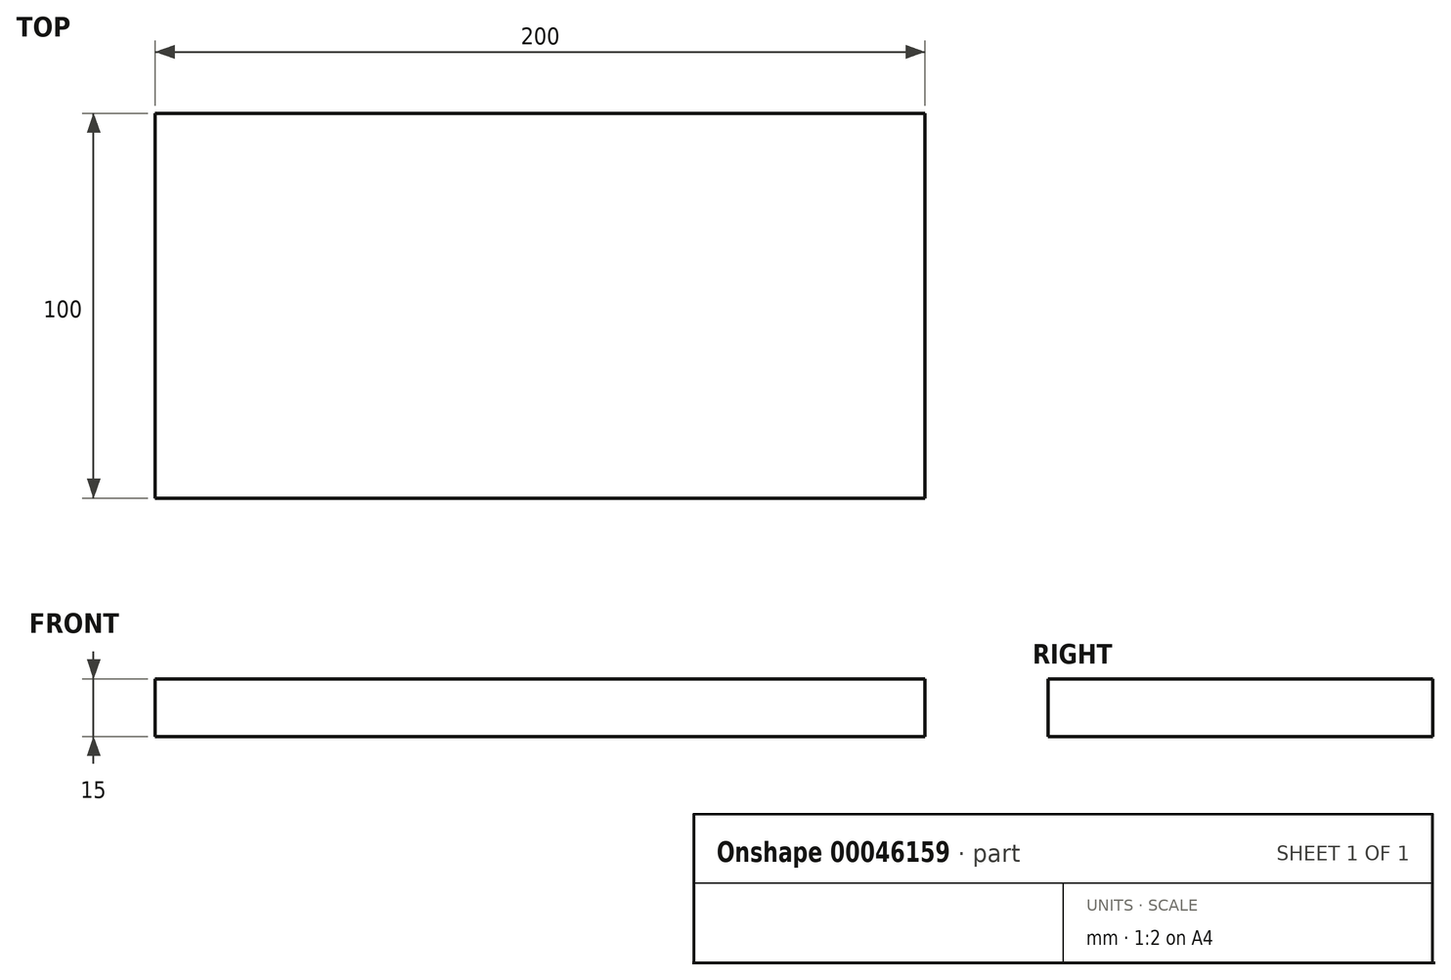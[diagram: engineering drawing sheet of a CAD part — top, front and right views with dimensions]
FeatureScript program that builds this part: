
annotation { "Feature Type Name" : "Feature", "Feature Type Description" : "" }
export const myFeature = defineFeature(function(context is Context, id is Id, definition is map)
    precondition{}
    {
        {
            var Q0;
            Q0=qCreatedBy(makeId("Top.planeOp"),FACE);
            var sketch = newSketch(context, id + "F0", { "sketchPlane" : qUnion([Q0])});
            skLineSegment(sketch, "E0.rect.bottom", {"start": v(100, 50) * mm, "end": v(-100, 50) * mm});
            skLineSegment(sketch, "E0.rect.top", {"start": v(100, -50) * mm, "end": v(-100, -50) * mm});
            skLineSegment(sketch, "E0.rect.left", {"start": v(100, 50) * mm, "end": v(100, -50) * mm});
            skLineSegment(sketch, "E0.rect.right", {"start": v(-100, 50) * mm, "end": v(-100, -50) * mm});
            skPoint(sketch, "E0.rect.middle", {"position": v(0, 0) * mm});
            skSolve(sketch);
        }
        {
            var Q0;
            Q0=makeQuery(id+"F0.imprint","IMPRINT",FACE,{"disambiguationData":[TD([[makeQuery(id+"F0.imprint","IMPRINT",EDGE,{"derivedFrom":sQuery(id+"F0.wireOp",EDGE,"E0.rect.bottom")}),1.0]])]});
            extrude(context, id + "F1", {"entities" : qUnion([Q0]), "depth" : 15 * mm});
        }
    });
